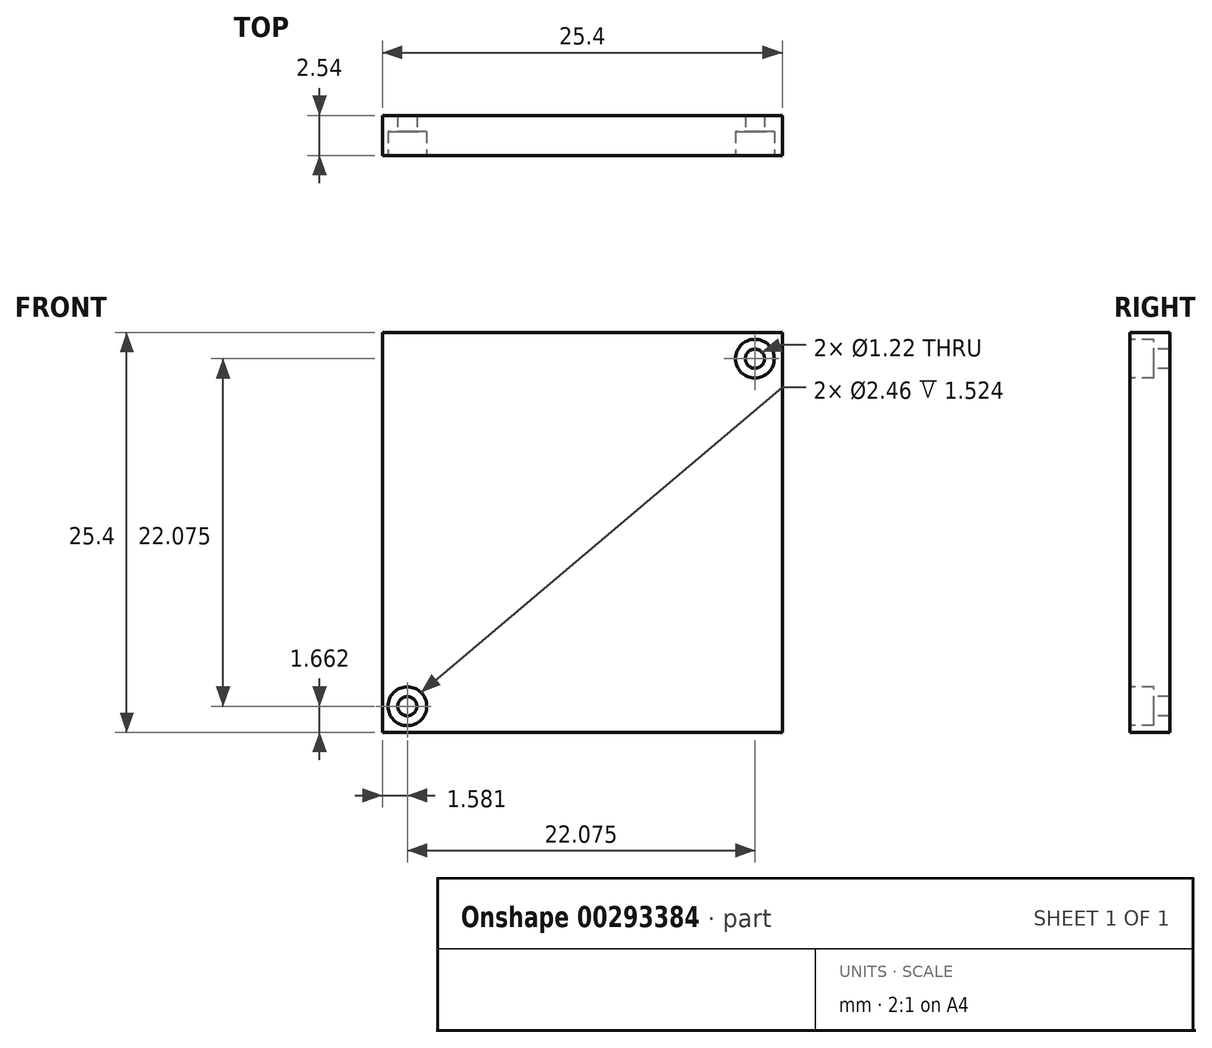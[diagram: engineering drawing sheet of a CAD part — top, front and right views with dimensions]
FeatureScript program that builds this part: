
annotation { "Feature Type Name" : "Feature", "Feature Type Description" : "" }
export const myFeature = defineFeature(function(context is Context, id is Id, definition is map)
    precondition{}
    {
        {
            var Q0;
            Q0=qCreatedBy(makeId("Front.planeOp"),FACE);
            var sketch = newSketch(context, id + "F0", { "sketchPlane" : qUnion([Q0])});
            skLineSegment(sketch, "E0.bottom", {"start": v(12.7, 12.7) * mm, "end": v(-12.7, 12.7) * mm});
            skLineSegment(sketch, "E0.top", {"start": v(12.7, -12.7) * mm, "end": v(-12.7, -12.7) * mm});
            skLineSegment(sketch, "E0.left", {"start": v(12.7, 12.7) * mm, "end": v(12.7, -12.7) * mm});
            skLineSegment(sketch, "E0.right", {"start": v(-12.7, 12.7) * mm, "end": v(-12.7, -12.7) * mm});
            skPoint(sketch, "E0.middle", {"position": v(0, 0) * mm});
            skSolve(sketch);
        }
        {
            var Q0;
            Q0=makeQuery(id+"F0.imprint","IMPRINT",FACE,{"disambiguationData":[TD([[makeQuery(id+"F0.imprint","IMPRINT",EDGE,{"derivedFrom":sQuery(id+"F0.wireOp",EDGE,"E0.bottom")}),1.0]])]});
            extrude(context, id + "F1", {"entities" : qUnion([Q0]), "depth" : 2.54 * mm});
        }
        {
            var Q0;
            Q0=makeQuery(id+"F1.opExtrude","CAP_FACE",FACE,{"disambiguationData":[OSD([sQuery(id+"F0.wireOp",EDGE,"E0.bottom"),sQuery(id+"F0.wireOp",EDGE,"E0.top"),sQuery(id+"F0.wireOp",EDGE,"E0.left"),sQuery(id+"F0.wireOp",EDGE,"E0.right")])],"isStart":false});
            var sketch = newSketch(context, id + "F2", { "sketchPlane" : qUnion([Q0])});
            skPoint(sketch, "E1", {"position": v(-11.12, -11.04) * mm});
            skPoint(sketch, "E2", {"position": v(10.96, 11.04) * mm});
            skSolve(sketch);
        }
        {
            var Q0;
            Q0=sQuery(id+"F2.wireOp",VERTEX,"E1");
            var Q1;
            Q1=makeQuery(id+"F1.opExtrude","SWEPT_BODY",BODY,{"disambiguationData":[OSD([sQuery(id+"F0.wireOp",EDGE,"E0.bottom"),sQuery(id+"F0.wireOp",EDGE,"E0.top"),sQuery(id+"F0.wireOp",EDGE,"E0.left"),sQuery(id+"F0.wireOp",EDGE,"E0.right")])]});
            hole(context, id + "F3", {"style" : HoleStyle.C_BORE, "endStyle" : HoleEndStyle.THROUGH, "holeDiameter" : 1.22 * mm, "cBoreDiameter" : 2.46 * mm, "cBoreDepth" : 1.52 * mm, "tappedDepth" : 12.7 * mm, "tapClearance" : 3, "startFromSketch" : true, "locations" : qUnion([Q0]), "scope" : qUnion([Q1])});
        }
        {
            var Q0;
            Q0=sQuery(id+"F2.wireOp",VERTEX,"E2");
            var Q1;
            Q1=makeQuery(id+"F1.opExtrude","SWEPT_BODY",BODY,{"disambiguationData":[OSD([sQuery(id+"F0.wireOp",EDGE,"E0.bottom"),sQuery(id+"F0.wireOp",EDGE,"E0.top"),sQuery(id+"F0.wireOp",EDGE,"E0.left"),sQuery(id+"F0.wireOp",EDGE,"E0.right")])]});
            hole(context, id + "F4", {"style" : HoleStyle.C_BORE, "endStyle" : HoleEndStyle.THROUGH, "holeDiameter" : 1.22 * mm, "cBoreDiameter" : 2.46 * mm, "cBoreDepth" : 1.52 * mm, "tappedDepth" : 12.7 * mm, "tapClearance" : 3, "startFromSketch" : true, "locations" : qUnion([Q0]), "scope" : qUnion([Q1])});
        }
    });
